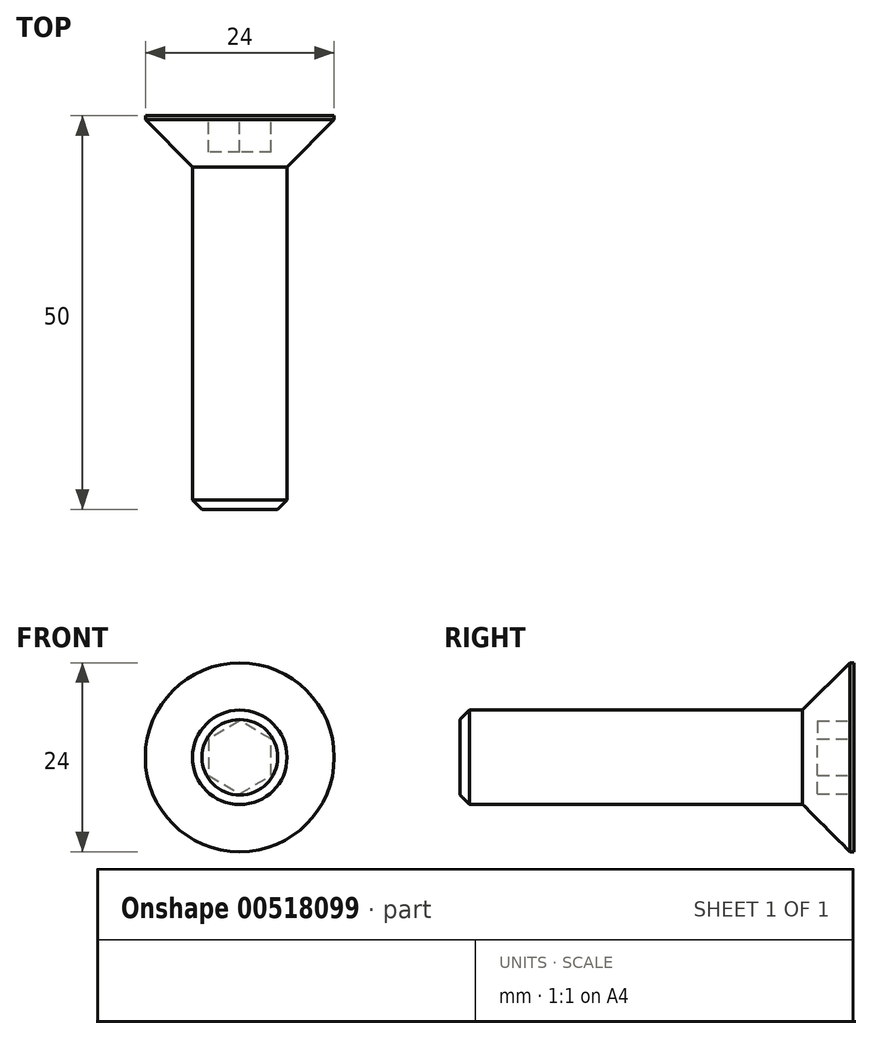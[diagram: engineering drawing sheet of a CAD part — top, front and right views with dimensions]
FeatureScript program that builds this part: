
annotation { "Feature Type Name" : "Feature", "Feature Type Description" : "" }
export const myFeature = defineFeature(function(context is Context, id is Id, definition is map)
    precondition{}
    {
        {
            assignVariable(context, id + "F0", {"name" : "t", "anyValue" : 4.6});
        }
        {
            var Q0;
            Q0=qCreatedBy(makeId("Right.planeOp"),FACE);
            var sketch = newSketch(context, id + "F1", { "sketchPlane" : qUnion([Q0])});
            skLineSegment(sketch, "E0", {"start": v(0, 0) * mm, "end": v(0, 12) * mm});
            skLineSegment(sketch, "E1", {"start": v(0, 12) * mm, "end": v(-0.5, 12) * mm});
            skLineSegment(sketch, "E2", {"start": v(-0.5, 12) * mm, "end": v(-6.5, 6) * mm});
            skLineSegment(sketch, "E3", {"start": v(-6.5, 6) * mm, "end": v(-48.8, 6) * mm});
            skLineSegment(sketch, "E4", {"start": v(-48.8, 6) * mm, "end": v(-50, 4.8) * mm});
            skLineSegment(sketch, "E5", {"start": v(-50, 4.8) * mm, "end": v(-50, 0) * mm});
            skLineSegment(sketch, "E6", {"start": v(-50, 0) * mm, "end": v(0, 0) * mm});
            skSolve(sketch);
        }
        {
            var Q0;
            Q0=makeQuery(id+"F1.imprint","IMPRINT",FACE,{"disambiguationData":[TD([[makeQuery(id+"F1.imprint","IMPRINT",EDGE,{"derivedFrom":sQuery(id+"F1.wireOp",EDGE,"E0")}),1.0]])]});
            var Q1;
            Q1=sQuery(id+"F1.wireOp",EDGE,"E6");
            revolve(context, id + "F2", {"entities" : qUnion([Q0]), "axis" : qUnion([Q1]), "revolveType" : RevolveType.FULL});
        }
        {
            var Q0;
            Q0=makeQuery(id+"F2.opRevolve","SWEPT_FACE",FACE,{"disambiguationData":[OSD([sQuery(id+"F1.wireOp",EDGE,"E0")])]});
            var sketch = newSketch(context, id + "F3", { "sketchPlane" : qUnion([Q0])});
            skCircle(sketch, "E7.cCircle", {"center": v(0, 0) * mm, "radius": 4.62 * mm, "construction": true});
            skLineSegment(sketch, "E7.0", {"start": v(0, 4.62) * mm, "end": v(4, 2.3) * mm});
            skLineSegment(sketch, "E7.1", {"start": v(4, 2.3) * mm, "end": v(4, -2.3) * mm});
            skLineSegment(sketch, "E7.2", {"start": v(4, -2.3) * mm, "end": v(0, -4.62) * mm});
            skLineSegment(sketch, "E7.3", {"start": v(0, -4.62) * mm, "end": v(-4, -2.3) * mm});
            skLineSegment(sketch, "E7.4", {"start": v(-4, -2.3) * mm, "end": v(-4, 2.3) * mm});
            skLineSegment(sketch, "E7.5", {"start": v(-4, 2.3) * mm, "end": v(0, 4.62) * mm});
            skSolve(sketch);
        }
        {
            var Q0;
            Q0 = qSketchRegion(id + "F3", true);
            extrude(context, id + "F4", {"entities" : qUnion([Q0]), "operationType" : NewBodyOperationType.REMOVE, "oppositeDirection" : true, "depth" : (getVariable(context, 't')) * mm, "offsetDistance" : 25 * mm});
        }
    });
